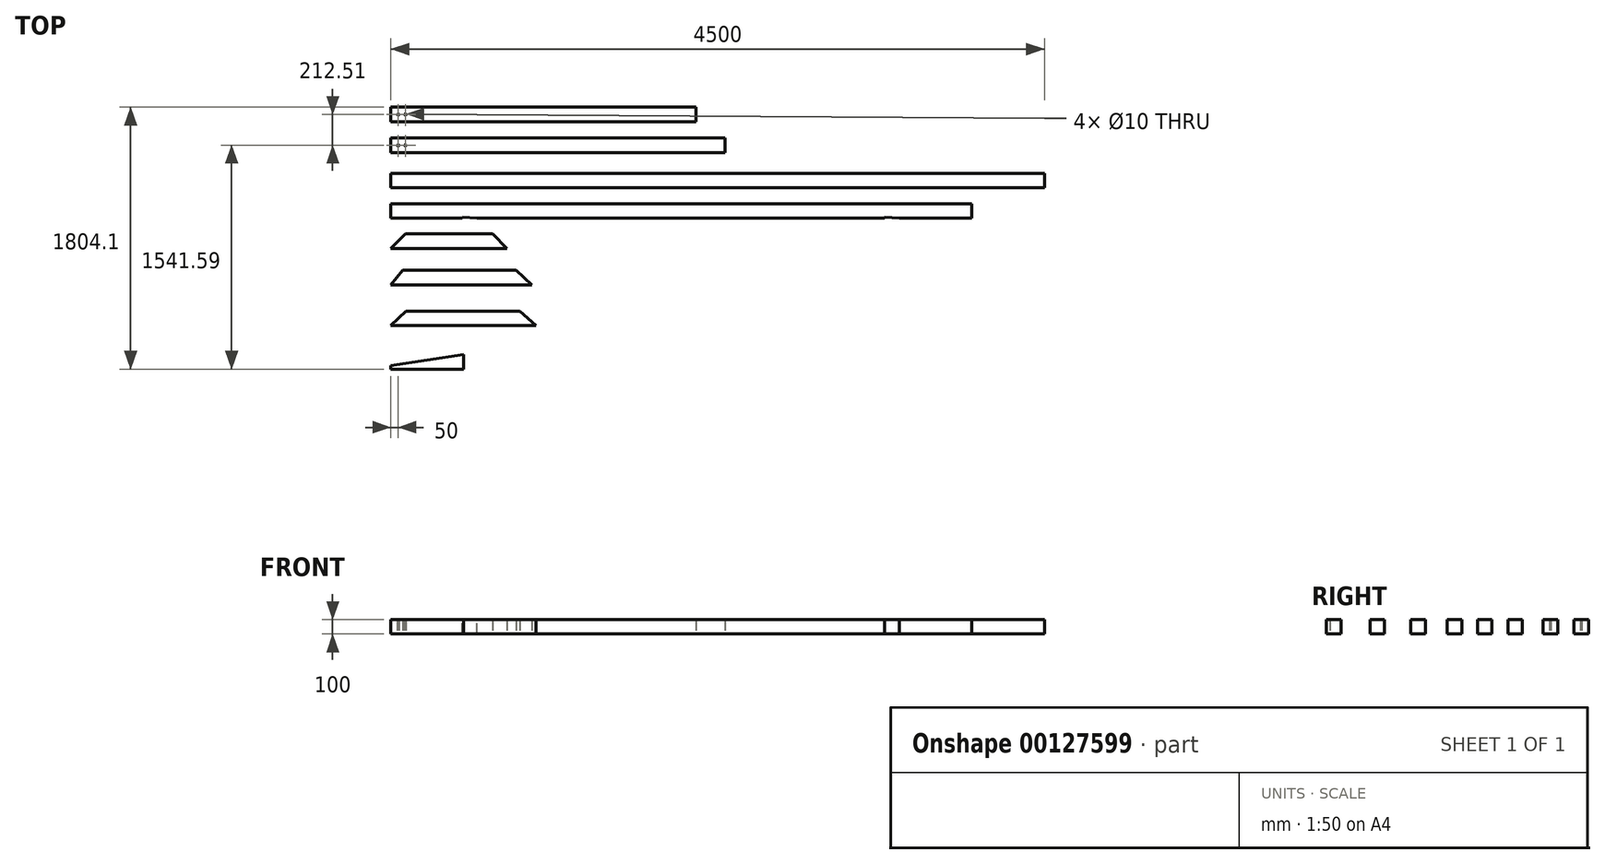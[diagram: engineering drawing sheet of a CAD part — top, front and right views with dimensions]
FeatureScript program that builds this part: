
annotation { "Feature Type Name" : "Feature", "Feature Type Description" : "" }
export const myFeature = defineFeature(function(context is Context, id is Id, definition is map)
    precondition{}
    {
        {
            var Q0;
            Q0=qCreatedBy(makeId("Top.planeOp"),FACE);
            var sketch = newSketch(context, id + "F0", { "sketchPlane" : qUnion([Q0])});
            skLineSegment(sketch, "E0.bottom", {"start": v(0, 100) * mm, "end": v(2100, 100) * mm});
            skLineSegment(sketch, "E0.top", {"start": v(0, 0) * mm, "end": v(2100, 0) * mm});
            skLineSegment(sketch, "E0.left", {"start": v(0, 100) * mm, "end": v(0, 0) * mm});
            skLineSegment(sketch, "E0.right", {"start": v(2100, 100) * mm, "end": v(2100, 0) * mm});
            skLineSegment(sketch, "E1.bottom", {"start": v(0, -112.51) * mm, "end": v(2300, -112.51) * mm});
            skLineSegment(sketch, "E1.top", {"start": v(0, -212.51) * mm, "end": v(2300, -212.51) * mm});
            skLineSegment(sketch, "E1.left", {"start": v(0, -112.51) * mm, "end": v(0, -212.51) * mm});
            skLineSegment(sketch, "E1.right", {"start": v(2300, -112.51) * mm, "end": v(2300, -212.51) * mm});
            skLineSegment(sketch, "E2", {"start": v(196.52, -162.51) * mm, "end": v(353.7, -162.51) * mm, "construction": true});
            skPoint(sketch, "E2.startSnap0", {"position": v(0, -162.51) * mm});
            skCircle(sketch, "E3", {"center": v(50, -162.51) * mm, "radius": 5 * mm});
            skCircle(sketch, "E4", {"center": v(100, -162.51) * mm, "radius": 5 * mm});
            skLineSegment(sketch, "E5", {"start": v(159.91, 50) * mm, "end": v(256.49, 50) * mm, "construction": true});
            skPoint(sketch, "E5.startSnap0", {"position": v(0, 50) * mm});
            skCircle(sketch, "E6", {"center": v(50, 50) * mm, "radius": 5 * mm});
            skCircle(sketch, "E7", {"center": v(100, 50) * mm, "radius": 5 * mm});
            skLineSegment(sketch, "E8.bottom", {"start": v(0, -354.4) * mm, "end": v(4500, -354.4) * mm});
            skLineSegment(sketch, "E8.left", {"start": v(0, -354.4) * mm, "end": v(0, -454.4) * mm});
            skLineSegment(sketch, "E9.bottom", {"start": v(0, -564.32) * mm, "end": v(4000, -564.32) * mm});
            skLineSegment(sketch, "E9.top", {"start": v(0, -664.32) * mm, "end": v(4000, -664.32) * mm});
            skLineSegment(sketch, "E9.left", {"start": v(0, -564.32) * mm, "end": v(0, -664.32) * mm});
            skLineSegment(sketch, "E9.right", {"start": v(4000, -564.32) * mm, "end": v(4000, -664.32) * mm});
            skLineSegment(sketch, "E10.top", {"start": v(0, -872.81) * mm, "end": v(800, -872.81) * mm});
            skLineSegment(sketch, "E11", {"start": v(0, -872.81) * mm, "end": v(100, -772.81) * mm});
            skLineSegment(sketch, "E12", {"start": v(800, -872.81) * mm, "end": v(700, -772.81) * mm});
            skLineSegment(sketch, "E13", {"start": v(100, -772.81) * mm, "end": v(700, -772.81) * mm});
            skLineSegment(sketch, "E14", {"start": v(0, -1122.97) * mm, "end": v(970, -1122.97) * mm});
            skLineSegment(sketch, "E15", {"start": v(970, -1122.97) * mm, "end": v(862.76, -1022.97) * mm});
            skLineSegment(sketch, "E16", {"start": v(862.76, -1022.97) * mm, "end": v(80.98, -1022.97) * mm});
            skLineSegment(sketch, "E17", {"start": v(80.98, -1022.97) * mm, "end": v(0, -1122.97) * mm});
            skLineSegment(sketch, "E18", {"start": v(0, -1404.66) * mm, "end": v(998, -1404.66) * mm});
            skLineSegment(sketch, "E19", {"start": v(998, -1404.66) * mm, "end": v(886.94, -1304.66) * mm});
            skLineSegment(sketch, "E20", {"start": v(886.94, -1304.66) * mm, "end": v(103.55, -1304.66) * mm});
            skLineSegment(sketch, "E21", {"start": v(103.55, -1304.66) * mm, "end": v(0, -1404.66) * mm});
            skLineSegment(sketch, "E22", {"start": v(0, -1704.1) * mm, "end": v(500, -1704.1) * mm});
            skLineSegment(sketch, "E23", {"start": v(500, -1704.1) * mm, "end": v(500, -1604.1) * mm});
            skLineSegment(sketch, "E24", {"start": v(500, -1604.1) * mm, "end": v(0, -1679.1) * mm});
            skLineSegment(sketch, "E25", {"start": v(0, -1679.1) * mm, "end": v(0, -1704.1) * mm});
            skLineSegment(sketch, "E26", {"start": v(1166.48, -1625.1) * mm, "end": v(1136.48, -1604.1) * mm});
            skLineSegment(sketch, "E27", {"start": v(736.48, -1604.1) * mm, "end": v(736.48, -1704.1) * mm});
            skLineSegment(sketch, "E28", {"start": v(736.48, -1604.1) * mm, "end": v(1136.48, -1604.1) * mm});
            skLineSegment(sketch, "E29", {"start": v(736.48, -1704.1) * mm, "end": v(1116.48, -1704.1) * mm});
            skLineSegment(sketch, "E30", {"start": v(1116.48, -1704.1) * mm, "end": v(1166.48, -1625.1) * mm});
            skLineSegment(sketch, "E31", {"start": v(4500, -454.4) * mm, "end": v(4500, -354.4) * mm});
            skLineSegment(sketch, "E32", {"start": v(4500, -454.4) * mm, "end": v(0, -454.4) * mm});
            skSolve(sketch);
        }
        {
            var Q0;
            Q0=makeQuery(id+"F0.imprint","IMPRINT",FACE,{"disambiguationData":[TD([[makeQuery(id+"F0.imprint","IMPRINT",EDGE,{"derivedFrom":sQuery(id+"F0.wireOp",EDGE,"E0.bottom")}),-1.0]])]});
            var Q1;
            Q1=makeQuery(id+"F0.imprint","IMPRINT",FACE,{"disambiguationData":[TD([[makeQuery(id+"F0.imprint","IMPRINT",EDGE,{"derivedFrom":sQuery(id+"F0.wireOp",EDGE,"E1.bottom")}),-1.0]])]});
            var Q2;
            Q2=makeQuery(id+"F0.imprint","IMPRINT",FACE,{"disambiguationData":[TD([[makeQuery(id+"F0.imprint","IMPRINT",EDGE,{"derivedFrom":sQuery(id+"F0.wireOp",EDGE,"E8.bottom")}),-1.0]])]});
            var Q3;
            Q3=makeQuery(id+"F0.imprint","IMPRINT",FACE,{"disambiguationData":[TD([[makeQuery(id+"F0.imprint","IMPRINT",EDGE,{"derivedFrom":sQuery(id+"F0.wireOp",EDGE,"E9.bottom")}),-1.0]])]});
            var Q4;
            Q4=makeQuery(id+"F0.imprint","IMPRINT",FACE,{"disambiguationData":[TD([[makeQuery(id+"F0.imprint","IMPRINT",EDGE,{"derivedFrom":sQuery(id+"F0.wireOp",EDGE,"E10.top")}),1.0]])]});
            var Q5;
            Q5=makeQuery(id+"F0.imprint","IMPRINT",FACE,{"disambiguationData":[TD([[makeQuery(id+"F0.imprint","IMPRINT",EDGE,{"derivedFrom":sQuery(id+"F0.wireOp",EDGE,"E14")}),1.0]])]});
            var Q6;
            Q6=makeQuery(id+"F0.imprint","IMPRINT",FACE,{"disambiguationData":[TD([[makeQuery(id+"F0.imprint","IMPRINT",EDGE,{"derivedFrom":sQuery(id+"F0.wireOp",EDGE,"E18")}),1.0]])]});
            var Q7;
            Q7=makeQuery(id+"F0.imprint","IMPRINT",FACE,{"disambiguationData":[TD([[makeQuery(id+"F0.imprint","IMPRINT",EDGE,{"derivedFrom":sQuery(id+"F0.wireOp",EDGE,"E22")}),1.0]])]});
            var Q8;
            Q8=makeQuery(id+"F0.imprint","IMPRINT",FACE,{"disambiguationData":[TD([[makeQuery(id+"F0.imprint","IMPRINT",EDGE,{"derivedFrom":sQuery(id+"F0.wireOp",EDGE,"0qvXEdDx-HD2A-Bvgd-4Dte-hPvKWJeQZIPT")}),1.0]])]});
            extrude(context, id + "F1", {"entities" : qUnion([Q0, Q1, Q2, Q3, Q4, Q5, Q6, Q7, Q8]), "depth" : 100 * mm});
        }
        {
            var Q0;
            Q0=makeQuery(id+"F1.opExtrude","SWEPT_FACE",FACE,{"disambiguationData":[OSD([sQuery(id+"F0.wireOp",EDGE,"E8.bottom")])]});
            var sketch = newSketch(context, id + "F2", { "sketchPlane" : qUnion([Q0])});
            skLineSegment(sketch, "E33", {"start": v(-2484.43, 50) * mm, "end": v(-2329.91, 50) * mm, "construction": true});
            skPoint(sketch, "E33.startSnap0", {"position": v(0, 50) * mm});
            skCircle(sketch, "E34", {"center": v(50, 50) * mm, "radius": 5 * mm});
            skCircle(sketch, "E35", {"center": v(100, 50) * mm, "radius": 5 * mm});
            skSolve(sketch);
        }
        {
            var Q0;
            Q0=makeQuery(id+"F2.imprint","IMPRINT",FACE,{"disambiguationData":[TD([[makeQuery(id+"F2.imprint","IMPRINT",EDGE,{"derivedFrom":sQuery(id+"F2.wireOp",EDGE,"E35")}),1.0]])]});
            var Q1;
            Q1=makeQuery(id+"F2.imprint","IMPRINT",FACE,{"disambiguationData":[TD([[makeQuery(id+"F2.imprint","IMPRINT",EDGE,{"derivedFrom":sQuery(id+"F2.wireOp",EDGE,"E34")}),1.0]])]});
            extrude(context, id + "F3", {"entities" : qUnion([Q0, Q1]), "operationType" : NewBodyOperationType.REMOVE, "oppositeDirection" : true, "depth" : 50 * mm});
        }
        {
            var Q0;
            Q0=makeQuery(id+"F1.opExtrude","CAP_FACE",FACE,{"disambiguationData":[OSD([sQuery(id+"F0.wireOp",EDGE,"E9.bottom"),sQuery(id+"F0.wireOp",EDGE,"E9.top"),sQuery(id+"F0.wireOp",EDGE,"E9.left"),sQuery(id+"F0.wireOp",EDGE,"E9.right")])],"isStart":false});
            var sketch = newSketch(context, id + "F4", { "sketchPlane" : qUnion([Q0])});
            skLineSegment(sketch, "E36", {"start": v(0, -1742.47) * mm, "end": v(4000, -1742.47) * mm, "construction": true});
            skLineSegment(sketch, "E37", {"start": v(4000, -1742.47) * mm, "end": v(4000, -1542.47) * mm, "construction": true});
            skLineSegment(sketch, "E38", {"start": v(0, -1742.47) * mm, "end": v(4000, -1542.47) * mm, "construction": true});
            skLineSegment(sketch, "E39", {"start": v(3400.24, -657.45) * mm, "end": v(3500, -664.32) * mm});
            skLineSegment(sketch, "E40", {"start": v(492.97, -657.45) * mm, "end": v(592.74, -664.32) * mm});
            skLineSegment(sketch, "E41", {"start": v(3400.24, -657.45) * mm, "end": v(3399.76, -664.32) * mm});
            skLineSegment(sketch, "E42", {"start": v(492.97, -657.45) * mm, "end": v(492.5, -664.32) * mm});
            skLineSegment(sketch, "E43", {"start": v(4000, -1542.47) * mm, "end": v(1548.9, -1542.47) * mm, "construction": true});
            skSolve(sketch);
        }
        {
            var Q0;
            {var subQ0=sQuery(id+"F4.wireOp",EDGE,"E39");Q0=makeQuery(id+"F4.imprint","IMPRINT",FACE,{"disambiguationData":[TD([[makeQuery(id+"F4.imprint","IMPRINT",EDGE,{"derivedFrom":subQ0}),-1.0]])]});}
            var Q1;
            {var subQ0=sQuery(id+"F4.wireOp",EDGE,"E40");Q1=makeQuery(id+"F4.imprint","IMPRINT",FACE,{"disambiguationData":[TD([[makeQuery(id+"F4.imprint","IMPRINT",EDGE,{"derivedFrom":subQ0}),-1.0]])]});}
            extrude(context, id + "F5", {"entities" : qUnion([Q0, Q1]), "operationType" : NewBodyOperationType.REMOVE, "oppositeDirection" : true, "depth" : 100 * mm});
        }
    });
